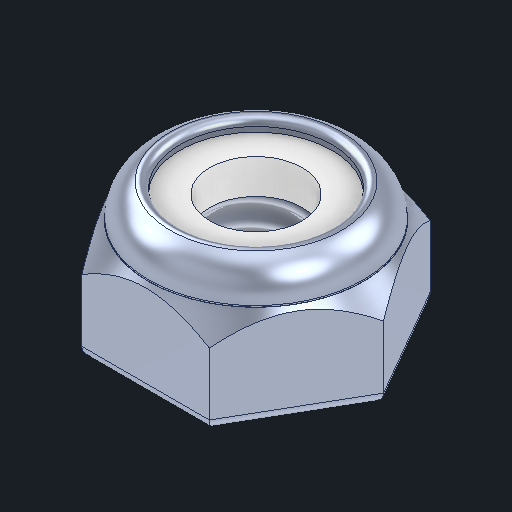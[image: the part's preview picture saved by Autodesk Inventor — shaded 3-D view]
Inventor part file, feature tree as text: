
AUTODESK INVENTOR PART (.ipt)
format: ipt  version: 2024 (Build 280153000, 153)  size: 227,840 bytes
history: native  units: in
note: dims shown in document units (in); Inventor stores cm internally (conversion verified against a paired STEP export)
features: other x4, sketch x2, plane x1
ambient origin geometry x8: Origin, YZ Plane, XZ Plane, XY Plane, X Axis, Y Axis, Z Axis, Center Point
bodies: Body1 (feature_tree)
feature tree (7):
  other  "Nut Thin Nylock.ipt"
  other  "NONE::Nut Thin Nylock.ipt"
  other  "TaggingFeature1"
  sketch  "Sketch1"  dims[d0=0.3937in]
  sketch  "Sketch2"
  plane  "Work Plane1"
  parser-record x1  (decoder bookkeeping rows leaked as tree rows — omitted from the tree; the rows remain in map.json)
